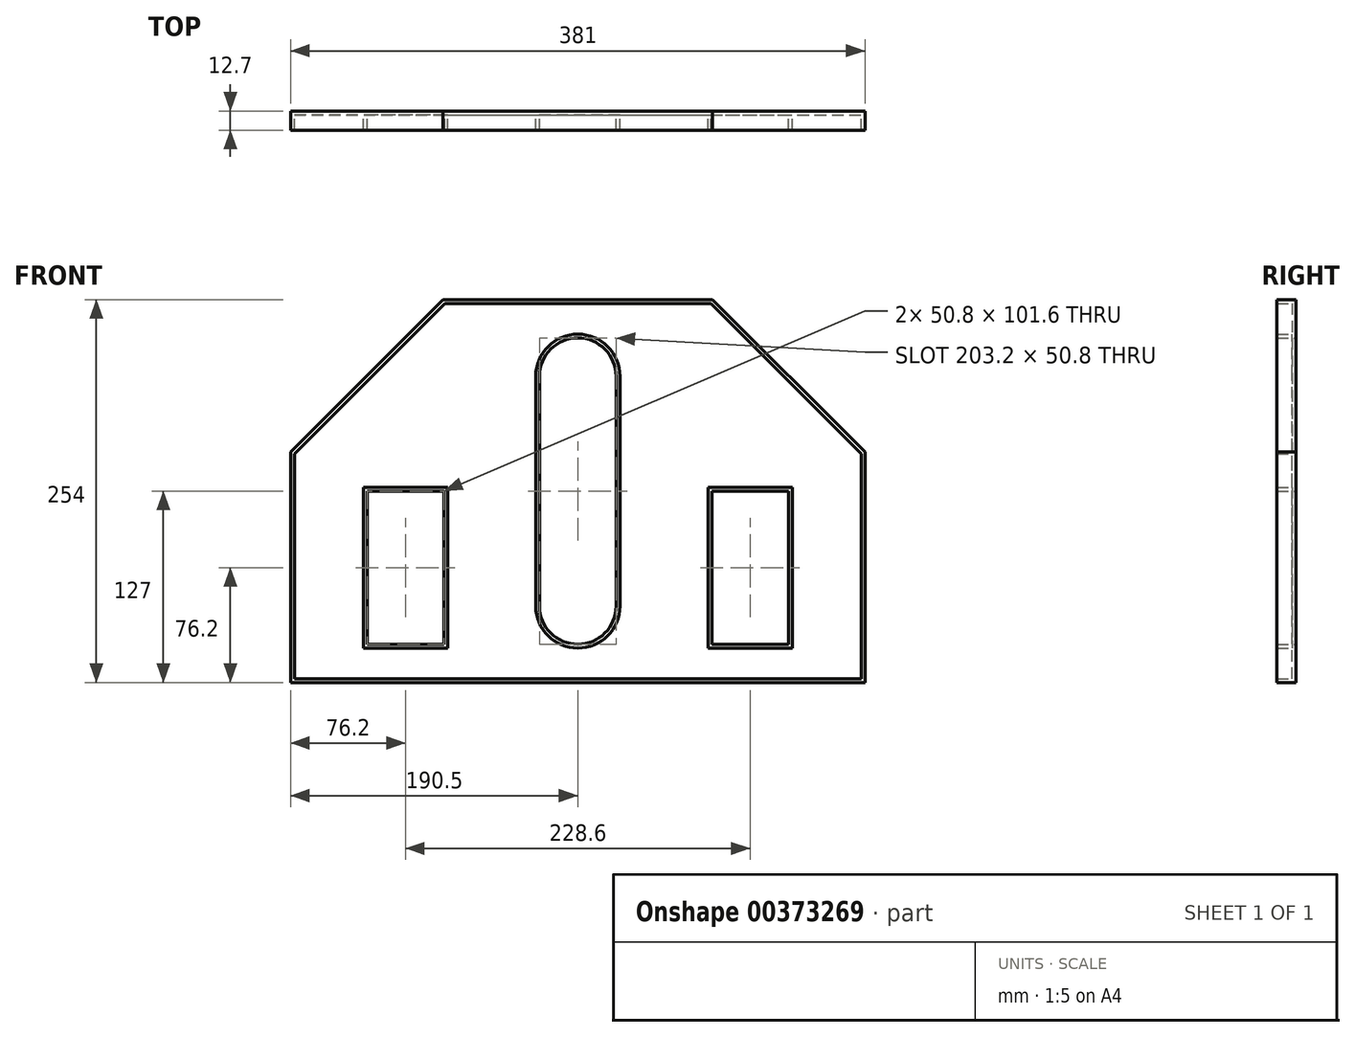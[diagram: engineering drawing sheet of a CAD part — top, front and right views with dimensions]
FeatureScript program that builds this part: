
annotation { "Feature Type Name" : "Feature", "Feature Type Description" : "" }
export const myFeature = defineFeature(function(context is Context, id is Id, definition is map)
    precondition{}
    {
        {
            var Q0;
            Q0=qCreatedBy(makeId("Front.planeOp"),FACE);
            var sketch = newSketch(context, id + "F0", { "sketchPlane" : qUnion([Q0])});
            skLineSegment(sketch, "E0.bottom", {"start": v(-190.5, -127) * mm, "end": v(190.5, -127) * mm});
            skLineSegment(sketch, "E0.top", {"start": v(-89.4, 127) * mm, "end": v(89.4, 127) * mm});
            skLineSegment(sketch, "E0.left", {"start": v(-190.5, -127) * mm, "end": v(-190.5, 25.9) * mm});
            skLineSegment(sketch, "E0.right", {"start": v(190.5, -127) * mm, "end": v(190.5, 25.9) * mm});
            skPoint(sketch, "E0.middle", {"position": v(0, 0) * mm});
            skPoint(sketch, "E1.startSnap0", {"position": v(0, 127) * mm});
            skLineSegment(sketch, "E2.bottom", {"start": v(88.9, 0) * mm, "end": v(139.7, 0) * mm});
            skLineSegment(sketch, "E2.top", {"start": v(88.9, -101.6) * mm, "end": v(139.7, -101.6) * mm});
            skLineSegment(sketch, "E2.left", {"start": v(88.9, 0) * mm, "end": v(88.9, -101.6) * mm});
            skLineSegment(sketch, "E2.right", {"start": v(139.7, 0) * mm, "end": v(139.7, -101.6) * mm});
            skLineSegment(sketch, "E3.MirrorCS", {"start": v(-88.9, 0) * mm, "end": v(-88.9, -101.6) * mm});
            skLineSegment(sketch, "E4.MirrorCS", {"start": v(-139.7, 0) * mm, "end": v(-139.7, -101.6) * mm});
            skLineSegment(sketch, "E5.MirrorCS", {"start": v(-88.9, 0) * mm, "end": v(-139.7, 0) * mm});
            skLineSegment(sketch, "E6.MirrorCS", {"start": v(-88.9, -101.6) * mm, "end": v(-139.7, -101.6) * mm});
            skPoint(sketch, "E7.endSnap0", {"position": v(-190.5, 0) * mm});
            skLineSegment(sketch, "E8.MirrorCS", {"start": v(-31.83, 76.2) * mm, "end": v(31.35, 76.2) * mm});
            skPoint(sketch, "E9", {"position": v(-89.4, 127) * mm});
            skPoint(sketch, "E10.MirrorP", {"position": v(89.4, 127) * mm});
            skLineSegment(sketch, "E11", {"start": v(-89.4, 127) * mm, "end": v(-190.5, 25.9) * mm});
            skPoint(sketch, "E12.orphan", {"position": v(-190.5, 127) * mm});
            skLineSegment(sketch, "E13.MirrorCS", {"start": v(89.4, 127) * mm, "end": v(190.5, 25.9) * mm});
            skArc(sketch, "E14", {"start": v(25.4, 76.2) * mm, "mid": v(0, 101.6) * mm, "end": v(-25.4, 76.2) * mm});
            skPoint(sketch, "E15.orphan", {"position": v(31.35, 76.2) * mm});
            skPoint(sketch, "E16.orphan", {"position": v(-31.83, 76.2) * mm});
            skPoint(sketch, "E17.orphan", {"position": v(-31.83, -76.2) * mm});
            skPoint(sketch, "E18.end.orphan", {"position": v(31.35, -76.2) * mm});
            skArc(sketch, "E19.MirrorCS", {"start": v(25.4, -76.2) * mm, "mid": v(0, -101.6) * mm, "end": v(-25.4, -76.2) * mm});
            skLineSegment(sketch, "E20.MirrorCS", {"start": v(-31.83, -76.2) * mm, "end": v(31.35, -76.2) * mm});
            skLineSegment(sketch, "E21", {"start": v(-25.4, -76.2) * mm, "end": v(-25.4, 76.2) * mm});
            skLineSegment(sketch, "E22", {"start": v(25.4, -76.2) * mm, "end": v(25.4, 76.2) * mm});
            skSolve(sketch);
        }
        {
            var Q0;
            Q0=makeQuery(id+"F0.imprint","IMPRINT",FACE,{"disambiguationData":[TD([[makeQuery(id+"F0.imprint","IMPRINT",EDGE,{"derivedFrom":sQuery(id+"F0.wireOp",EDGE,"E0.bottom")}),1.0]])]});
            extrude(context, id + "F1", {"entities" : qUnion([Q0]), "depth" : 12.7 * mm});
        }
        {
            var Q0;
            Q0=makeQuery(id+"F1.opExtrude","CAP_FACE",FACE,{"disambiguationData":[OSD([sQuery(id+"F0.wireOp",EDGE,"E0.bottom"),sQuery(id+"F0.wireOp",EDGE,"E0.top"),sQuery(id+"F0.wireOp",EDGE,"E0.left"),sQuery(id+"F0.wireOp",EDGE,"E0.right"),sQuery(id+"F0.wireOp",EDGE,"E2.bottom"),sQuery(id+"F0.wireOp",EDGE,"E2.top"),sQuery(id+"F0.wireOp",EDGE,"E2.left"),sQuery(id+"F0.wireOp",EDGE,"E2.right"),sQuery(id+"F0.wireOp",EDGE,"E3.MirrorCS"),sQuery(id+"F0.wireOp",EDGE,"E4.MirrorCS"),sQuery(id+"F0.wireOp",EDGE,"E5.MirrorCS"),sQuery(id+"F0.wireOp",EDGE,"E6.MirrorCS"),sQuery(id+"F0.wireOp",EDGE,"E11"),sQuery(id+"F0.wireOp",EDGE,"E13.MirrorCS"),sQuery(id+"F0.wireOp",EDGE,"E14"),sQuery(id+"F0.wireOp",EDGE,"E19.MirrorCS"),sQuery(id+"F0.wireOp",EDGE,"E21"),sQuery(id+"F0.wireOp",EDGE,"E22")])],"isStart":false});
            shell(context, id + "F2", {"entities" : qUnion([Q0]), "thickness" : 2.54 * mm});
        }
    });
